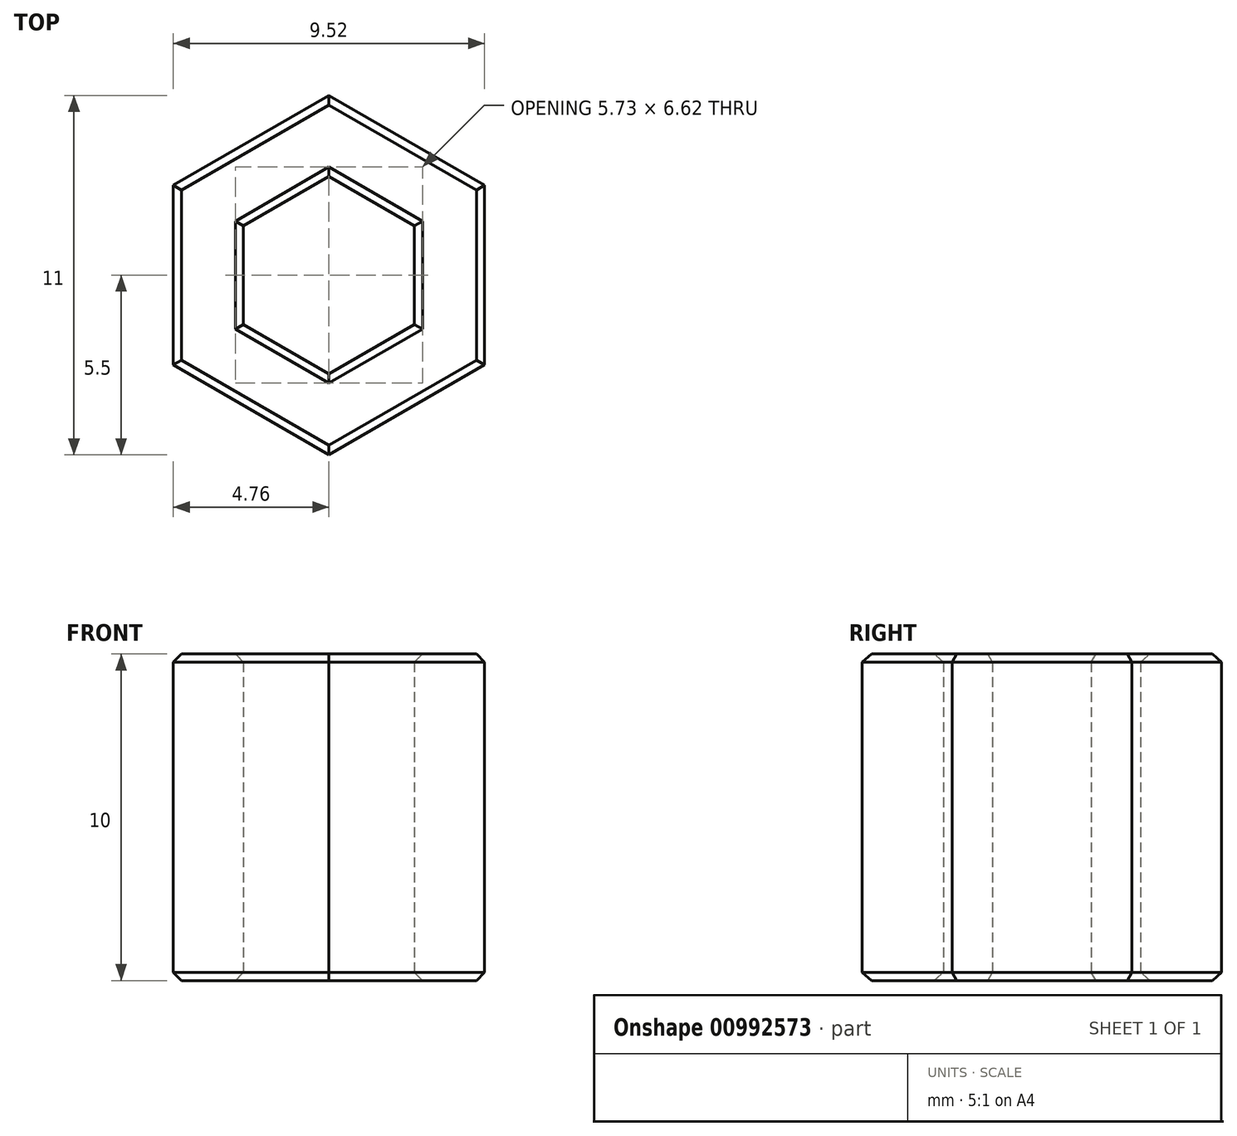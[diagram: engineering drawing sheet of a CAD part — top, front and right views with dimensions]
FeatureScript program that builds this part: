
annotation { "Feature Type Name" : "Feature", "Feature Type Description" : "" }
export const myFeature = defineFeature(function(context is Context, id is Id, definition is map)
    precondition{}
    {
        {
            var Q0;
            Q0=qCreatedBy(makeId("Top.planeOp"),FACE);
            var sketch = newSketch(context, id + "F0", { "sketchPlane" : qUnion([Q0])});
            skCircle(sketch, "E0.cCircle", {"center": v(0, 0) * mm, "radius": 2.62 * mm, "construction": true});
            skLineSegment(sketch, "E0.0", {"start": v(2.62, 1.5) * mm, "end": v(2.62, -1.5) * mm});
            skLineSegment(sketch, "E0.1", {"start": v(2.61, -1.5) * mm, "end": v(0, -3.02) * mm});
            skLineSegment(sketch, "E0.2", {"start": v(0, -3.02) * mm, "end": v(-2.62, -1.5) * mm});
            skLineSegment(sketch, "E0.3", {"start": v(-2.61, -1.5) * mm, "end": v(-2.62, 1.5) * mm});
            skLineSegment(sketch, "E0.4", {"start": v(-2.62, 1.5) * mm, "end": v(0, 3.02) * mm});
            skLineSegment(sketch, "E0.5", {"start": v(0, 3.02) * mm, "end": v(2.62, 1.5) * mm});
            skPoint(sketch, "E0.0.midPoint", {"position": v(2.62, 0) * mm});
            skCircle(sketch, "E1.cCircle", {"center": v(0, 0) * mm, "radius": 4.76 * mm, "construction": true});
            skLineSegment(sketch, "E1.0", {"start": v(4.76, 2.75) * mm, "end": v(4.76, -2.75) * mm});
            skLineSegment(sketch, "E1.1", {"start": v(4.76, -2.75) * mm, "end": v(0, -5.5) * mm});
            skLineSegment(sketch, "E1.2", {"start": v(0, -5.5) * mm, "end": v(-4.76, -2.75) * mm});
            skLineSegment(sketch, "E1.3", {"start": v(-4.76, -2.75) * mm, "end": v(-4.76, 2.75) * mm});
            skLineSegment(sketch, "E1.4", {"start": v(-4.76, 2.75) * mm, "end": v(0, 5.5) * mm});
            skLineSegment(sketch, "E1.5", {"start": v(0, 5.5) * mm, "end": v(4.76, 2.75) * mm});
            skPoint(sketch, "E1.0.midPoint", {"position": v(4.76, 0) * mm});
            skSolve(sketch);
        }
        {
            var Q0;
            Q0=makeQuery(id+"F0.imprint","IMPRINT",FACE,{"disambiguationData":[TD([[makeQuery(id+"F0.imprint","IMPRINT",EDGE,{"derivedFrom":sQuery(id+"F0.wireOp",EDGE,"E0.0")}),1.0]])]});
            extrude(context, id + "F1", {"entities" : qUnion([Q0]), "depth" : 10 * mm, "offsetDistance" : 25 * mm});
        }
        {
            var Q0;
            Q0=makeQuery(id+"F1.opExtrude","CAP_EDGE",EDGE,{"disambiguationData":[OSD([sQuery(id+"F0.wireOp",EDGE,"E1.2")])],"isStart":false});
            var Q1;
            Q1=makeQuery(id+"F1.opExtrude","CAP_EDGE",EDGE,{"disambiguationData":[OSD([sQuery(id+"F0.wireOp",EDGE,"E1.1")])],"isStart":false});
            var Q2;
            Q2=makeQuery(id+"F1.opExtrude","CAP_EDGE",EDGE,{"disambiguationData":[OSD([sQuery(id+"F0.wireOp",EDGE,"E1.0")])],"isStart":false});
            var Q3;
            Q3=makeQuery(id+"F1.opExtrude","CAP_EDGE",EDGE,{"disambiguationData":[OSD([sQuery(id+"F0.wireOp",EDGE,"E1.5")])],"isStart":false});
            var Q4;
            Q4=makeQuery(id+"F1.opExtrude","CAP_EDGE",EDGE,{"disambiguationData":[OSD([sQuery(id+"F0.wireOp",EDGE,"E0.4")])],"isStart":false});
            var Q5;
            Q5=makeQuery(id+"F1.opExtrude","CAP_EDGE",EDGE,{"disambiguationData":[OSD([sQuery(id+"F0.wireOp",EDGE,"E0.2")])],"isStart":false});
            var Q6;
            Q6=makeQuery(id+"F1.opExtrude","CAP_EDGE",EDGE,{"disambiguationData":[OSD([sQuery(id+"F0.wireOp",EDGE,"E0.0")])],"isStart":false});
            var Q7;
            Q7=makeQuery(id+"F1.opExtrude","CAP_EDGE",EDGE,{"disambiguationData":[OSD([sQuery(id+"F0.wireOp",EDGE,"E1.3")])],"isStart":false});
            var Q8;
            Q8=makeQuery(id+"F1.opExtrude","CAP_EDGE",EDGE,{"disambiguationData":[OSD([sQuery(id+"F0.wireOp",EDGE,"E0.3")])],"isStart":false});
            var Q9;
            Q9=makeQuery(id+"F1.opExtrude","CAP_EDGE",EDGE,{"disambiguationData":[OSD([sQuery(id+"F0.wireOp",EDGE,"E1.4")])],"isStart":false});
            var Q10;
            Q10=makeQuery(id+"F1.opExtrude","CAP_EDGE",EDGE,{"disambiguationData":[OSD([sQuery(id+"F0.wireOp",EDGE,"E0.5")])],"isStart":false});
            var Q11;
            Q11=makeQuery(id+"F1.opExtrude","CAP_EDGE",EDGE,{"disambiguationData":[OSD([sQuery(id+"F0.wireOp",EDGE,"E0.1")])],"isStart":false});
            var Q12;
            Q12=makeQuery(id+"F1.opExtrude","CAP_EDGE",EDGE,{"disambiguationData":[OSD([sQuery(id+"F0.wireOp",EDGE,"E0.3")])],"isStart":true});
            var Q13;
            Q13=makeQuery(id+"F1.opExtrude","CAP_EDGE",EDGE,{"disambiguationData":[OSD([sQuery(id+"F0.wireOp",EDGE,"E0.2")])],"isStart":true});
            var Q14;
            Q14=makeQuery(id+"F1.opExtrude","CAP_EDGE",EDGE,{"disambiguationData":[OSD([sQuery(id+"F0.wireOp",EDGE,"E1.5")])],"isStart":true});
            var Q15;
            Q15=makeQuery(id+"F1.opExtrude","CAP_EDGE",EDGE,{"disambiguationData":[OSD([sQuery(id+"F0.wireOp",EDGE,"E0.4")])],"isStart":true});
            var Q16;
            Q16=makeQuery(id+"F1.opExtrude","CAP_EDGE",EDGE,{"disambiguationData":[OSD([sQuery(id+"F0.wireOp",EDGE,"E1.2")])],"isStart":true});
            var Q17;
            Q17=makeQuery(id+"F1.opExtrude","CAP_EDGE",EDGE,{"disambiguationData":[OSD([sQuery(id+"F0.wireOp",EDGE,"E0.1")])],"isStart":true});
            var Q18;
            Q18=makeQuery(id+"F1.opExtrude","CAP_EDGE",EDGE,{"disambiguationData":[OSD([sQuery(id+"F0.wireOp",EDGE,"E1.0")])],"isStart":true});
            var Q19;
            Q19=makeQuery(id+"F1.opExtrude","CAP_EDGE",EDGE,{"disambiguationData":[OSD([sQuery(id+"F0.wireOp",EDGE,"E1.3")])],"isStart":true});
            var Q20;
            Q20=makeQuery(id+"F1.opExtrude","CAP_EDGE",EDGE,{"disambiguationData":[OSD([sQuery(id+"F0.wireOp",EDGE,"E1.4")])],"isStart":true});
            var Q21;
            Q21=makeQuery(id+"F1.opExtrude","CAP_EDGE",EDGE,{"disambiguationData":[OSD([sQuery(id+"F0.wireOp",EDGE,"E0.0")])],"isStart":true});
            var Q22;
            Q22=makeQuery(id+"F1.opExtrude","CAP_EDGE",EDGE,{"disambiguationData":[OSD([sQuery(id+"F0.wireOp",EDGE,"E1.1")])],"isStart":true});
            var Q23;
            Q23=makeQuery(id+"F1.opExtrude","CAP_EDGE",EDGE,{"disambiguationData":[OSD([sQuery(id+"F0.wireOp",EDGE,"E0.5")])],"isStart":true});
            chamfer(context, id + "F2", {"entities" : qUnion([Q0, Q1, Q2, Q3, Q4, Q5, Q6, Q7, Q8, Q9, Q10, Q11, Q12, Q13, Q14, Q15, Q16, Q17, Q18, Q19, Q20, Q21, Q22, Q23]), "width" : .25 * mm, "tangentPropagation" : true});
        }
    });
